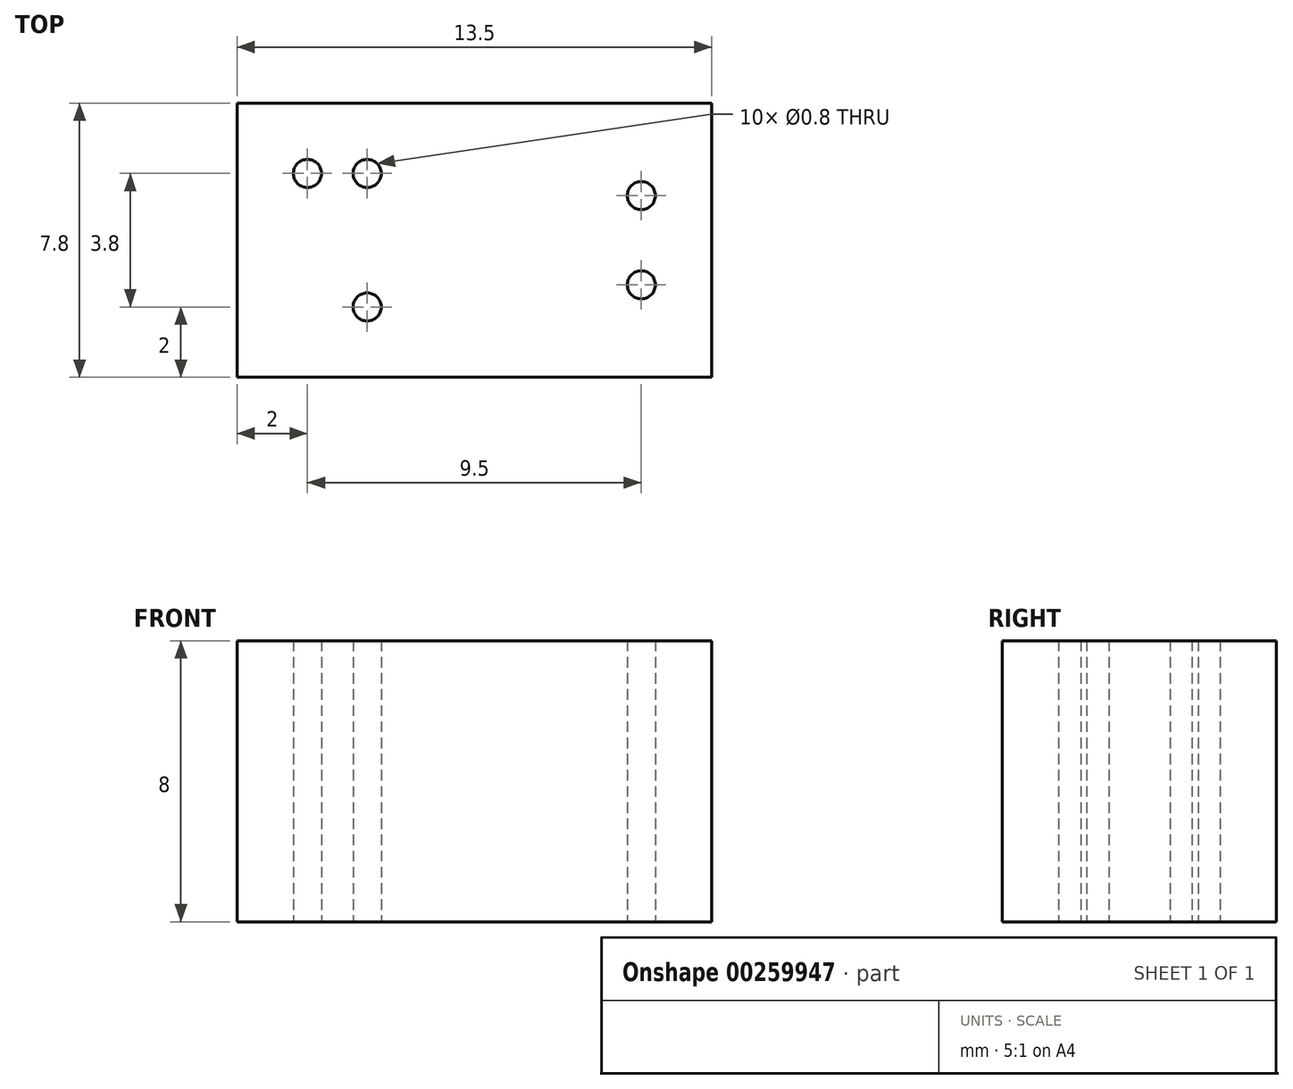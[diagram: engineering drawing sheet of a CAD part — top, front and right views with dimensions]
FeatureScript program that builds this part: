
annotation { "Feature Type Name" : "Feature", "Feature Type Description" : "" }
export const myFeature = defineFeature(function(context is Context, id is Id, definition is map)
    precondition{}
    {
        {
            var Q0;
            Q0=qCreatedBy(makeId("Top.planeOp"),FACE);
            var sketch = newSketch(context, id + "F0", { "sketchPlane" : qUnion([Q0])});
            skLineSegment(sketch, "E0.bottom", {"start": v(6.75, -3.9) * mm, "end": v(-6.75, -3.9) * mm});
            skLineSegment(sketch, "E0.top", {"start": v(6.75, 3.9) * mm, "end": v(-6.75, 3.9) * mm});
            skLineSegment(sketch, "E0.left", {"start": v(6.75, -3.9) * mm, "end": v(6.75, 3.9) * mm});
            skLineSegment(sketch, "E0.right", {"start": v(-6.75, -3.9) * mm, "end": v(-6.75, 3.9) * mm});
            skPoint(sketch, "E0.middle", {"position": v(0, 0) * mm});
            skCircle(sketch, "E1", {"center": v(-4.75, 1.9) * mm, "radius": 0.4 * mm});
            skCircle(sketch, "E2", {"center": v(-3.05, 1.9) * mm, "radius": 0.4 * mm});
            skCircle(sketch, "E3", {"center": v(-3.05, -1.9) * mm, "radius": 0.4 * mm});
            skCircle(sketch, "E4", {"center": v(4.75, 1.27) * mm, "radius": 0.4 * mm});
            skCircle(sketch, "E5", {"center": v(4.75, -1.27) * mm, "radius": 0.4 * mm});
            skSolve(sketch);
        }
        {
            var Q0;
            Q0 = qSketchRegion(id + "F0", true);
            extrude(context, id + "F1", {"entities" : qUnion([Q0]), "depth" : 8 * mm});
        }
    });
